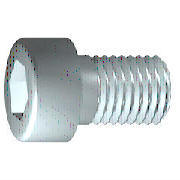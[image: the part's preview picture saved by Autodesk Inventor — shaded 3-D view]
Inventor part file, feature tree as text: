
AUTODESK INVENTOR PART (.ipt)
format: ipt  version: 2020 (Build 240168000, 168)  size: 188,928 bytes
history: native  units: mm (DEFAULTED — no unit token found)
features: sketch x2, other x1, extrude x1, plane x1, fillet x1
ambient origin geometry x7: Origin, YZ Plane, XY Plane, X Axis, Y Axis, Z Axis, Center Point
bodies: Solid1 (feature_tree)
feature tree (6):
  other  "Bryła"
  extrude  "Szczelina"  Depth=22.0mm
  plane  "Work Plane1"
  fillet  "Fillet2"  Radius=0.49086mm
  sketch  "Szkic1"
  sketch  "Szkic2"
